# Revit family: ASL_Designline_Head & Floor Track_64mm_Stud
name_source: partatom
category: Detail Items
revit_build: Autodesk Revit 2018 (Build: 20170223_1515(x64)
units: mm (PartAtom-declared; Revit-internal decimal feet)

## family parameters
Rotate with component = No
Section Shape = Not Defined
Shared = Yes

## types (4) — shared parameters
ASL 405 = No
Manufacturer = Aluminate Solutions Limited
Technical Info = www.aluminate.nz

## per-type parameters (varying)
| type | 13mm Plasterboard | 18mm Plasterboard | ASL 400 | ASL 400a | ASL 407 | ASL 410 | Head Depth | Masking Region Parametric | Type Comments |
| ASL 400a Head & Floor Track 64mm Stud 13mm Gib BS | Yes | No | No | Yes | No | No | 20 mm  [stored 0.0656168 ft] | 52 mm | ASL Designline ASL 400a Headsection With 64mm Stud 13mm Gib Bothside Wall |
| ASL 410 Head & Floor Track 64mm Stud 18mm Gib BS | No | Yes | No | No | No | Yes | 20 mm  [stored 0.0656168 ft] | 57 mm  [stored 0.187008 ft] | ASL Designline ASL 410 Headsection With 64mm Stud 18mm Gib Bothside Wall |
| ASL 407 Shadowline Head & Floor Track 64mm Stud 13mm Gib BS | Yes | No | No | No | Yes | No | 36 mm  [stored 0.11811 ft] | 52 mm | ASL Designline ASL 407 Shadowline Headsection With 64mm Stud 13mm Gib Bothside Wall |
| ASL 400 Head & Floor Track 64mm Stud 13mm Gib BS | Yes | No | Yes | No | No | No | 20 mm  [stored 0.0656168 ft] | 52 mm | ASL Designline ASL 400 Headsection With 64mm stud 13mm Gib Bothside Wall |

note: [stored X ft] marks values corroborated as IEEE doubles in the binary element streams (Revit-internal decimal feet)

## geometry (parser evidence)
native form markers: Sweep x4
no freeform markers — native parametric forms only
